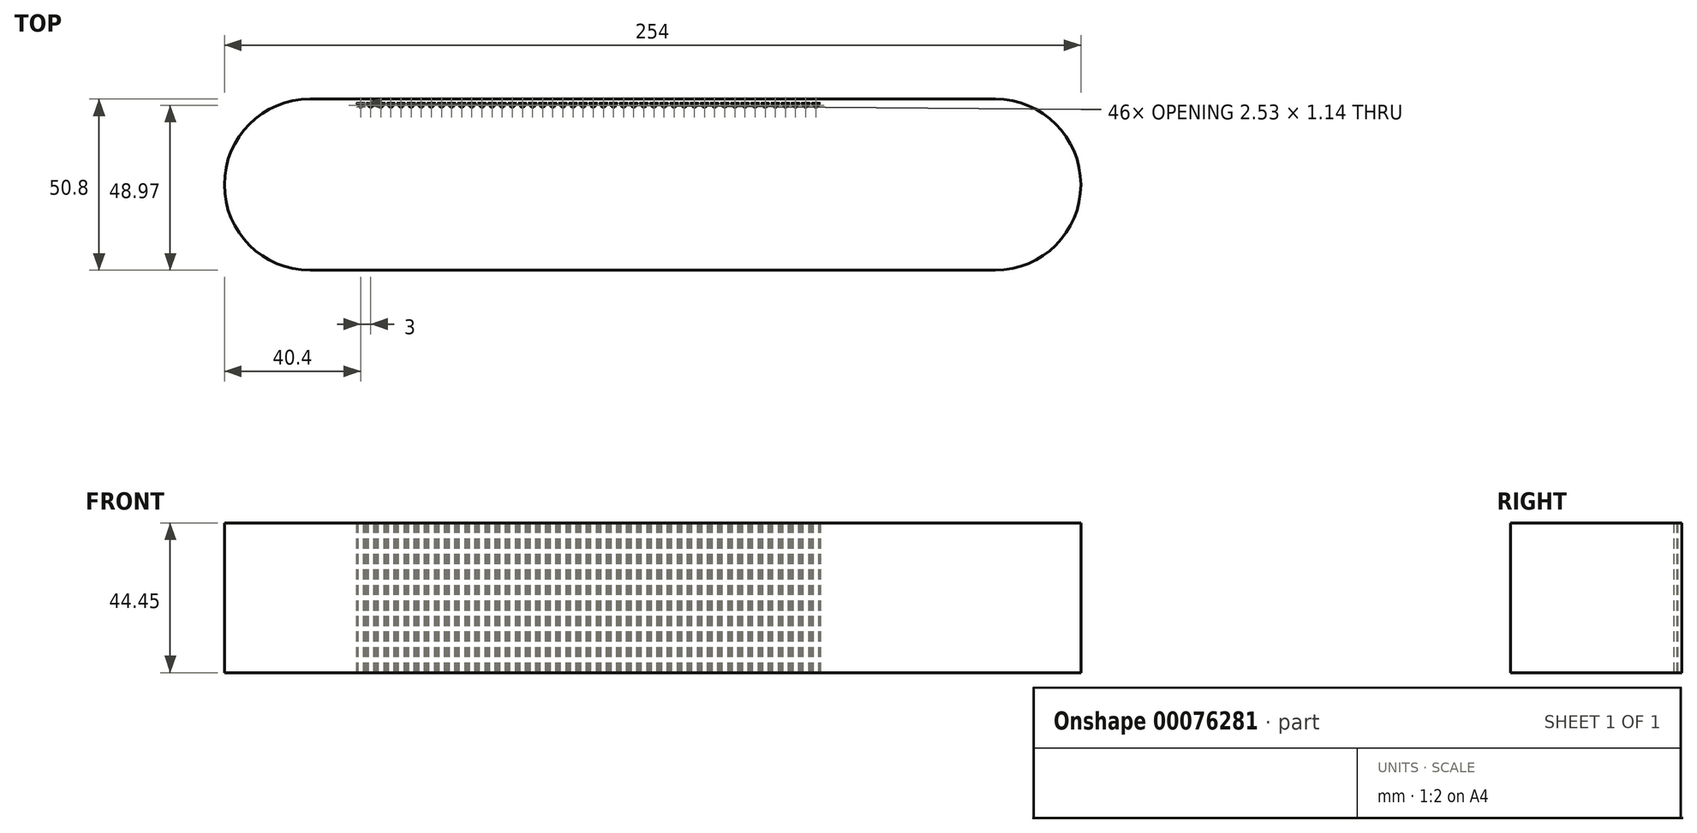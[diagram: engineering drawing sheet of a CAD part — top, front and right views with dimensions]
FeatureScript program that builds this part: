
annotation { "Feature Type Name" : "Feature", "Feature Type Description" : "" }
export const myFeature = defineFeature(function(context is Context, id is Id, definition is map)
    precondition{}
    {
        {
            var Q0;
            Q0=qCreatedBy(makeId("Top.planeOp"),FACE);
            var sketch = newSketch(context, id + "F0", { "sketchPlane" : qUnion([Q0])});
            skLineSegment(sketch, "E0.bottom", {"start": v(-101.6, -25.4) * mm, "end": v(101.6, -25.4) * mm});
            skLineSegment(sketch, "E0.top", {"start": v(-101.6, 25.4) * mm, "end": v(101.6, 25.4) * mm});
            skPoint(sketch, "E0.middle", {"position": v(0, 0) * mm});
            skArc(sketch, "E1", {"start": v(101.6, -25.4) * mm, "mid": v(127, 0) * mm, "end": v(101.6, 25.4) * mm});
            skArc(sketch, "E2", {"start": v(-101.6, 25.4) * mm, "mid": v(-127, 0) * mm, "end": v(-101.6, -25.4) * mm});
            skArc(sketch, "E3.0", {"start": v(-102.73, 24.11) * mm, "mid": v(-125.73, -0.57) * mm, "end": v(-101.6, -24.14) * mm});
            skLineSegment(sketch, "E3.1", {"start": v(-100.33, 24.14) * mm, "end": v(-99.87, 24.14) * mm});
            skArc(sketch, "E3.2", {"start": v(101.6, -24.14) * mm, "mid": v(125.74, 0) * mm, "end": v(101.6, 24.14) * mm});
            skLineSegment(sketch, "E3.3", {"start": v(-101.6, -24.14) * mm, "end": v(101.6, -24.14) * mm});
            skLineSegment(sketch, "E4", {"start": v(-101.6, 25.4) * mm, "end": v(-101.6, 23) * mm, "construction": true});
            skLineSegment(sketch, "E5", {"start": v(-101.6, 23) * mm, "end": v(-98.6, 23) * mm, "construction": true});
            skLineSegment(sketch, "E6", {"start": v(-98.6, 23) * mm, "end": v(-98.6, 23.85) * mm, "construction": true});
            skArc(sketch, "E7", {"start": v(-99.45, 23.78) * mm, "mid": v(-98.6, 23) * mm, "end": v(-97.75, 23.78) * mm});
            skLineSegment(sketch, "E8", {"start": v(-98.6, 23.85) * mm, "end": v(-101.6, 23.85) * mm, "construction": true});
            skArc(sketch, "E9", {"start": v(-102.45, 23.78) * mm, "mid": v(-101.6, 23) * mm, "end": v(-100.75, 23.78) * mm});
            skArc(sketch, "E10", {"start": v(-99.45, 23.78) * mm, "mid": v(-99.6, 24.03) * mm, "end": v(-99.87, 24.14) * mm});
            skArc(sketch, "E11.MirrorCS", {"start": v(-97.75, 23.78) * mm, "mid": v(-97.6, 24.03) * mm, "end": v(-97.33, 24.14) * mm});
            skLineSegment(sketch, "E12", {"start": v(-100.1, 23) * mm, "end": v(-100.1, 25.4) * mm, "construction": true});
            skArc(sketch, "E13.MirrorCS", {"start": v(-100.75, 23.78) * mm, "mid": v(-100.6, 24.03) * mm, "end": v(-100.33, 24.14) * mm});
            skArc(sketch, "E14.MirrorCS", {"start": v(-102.45, 23.78) * mm, "mid": v(-102.55, 23.98) * mm, "end": v(-102.73, 24.11) * mm});
            skPoint(sketch, "E15.orphan", {"position": v(-102.87, 24.14) * mm});
            skArc(sketch, "E16.1.0.0", {"start": v(-94.75, 23.78) * mm, "mid": v(-94.6, 24.03) * mm, "end": v(-94.33, 24.14) * mm});
            skArc(sketch, "E16.1.0.1", {"start": v(-96.45, 23.78) * mm, "mid": v(-95.6, 23) * mm, "end": v(-94.75, 23.78) * mm});
            skArc(sketch, "E16.1.0.2", {"start": v(-96.45, 23.78) * mm, "mid": v(-96.6, 24.03) * mm, "end": v(-96.87, 24.14) * mm});
            skArc(sketch, "E16.2.0.0", {"start": v(-91.75, 23.78) * mm, "mid": v(-91.6, 24.03) * mm, "end": v(-91.33, 24.14) * mm});
            skArc(sketch, "E16.2.0.1", {"start": v(-93.45, 23.78) * mm, "mid": v(-92.6, 23) * mm, "end": v(-91.75, 23.78) * mm});
            skArc(sketch, "E16.2.0.2", {"start": v(-93.45, 23.78) * mm, "mid": v(-93.6, 24.03) * mm, "end": v(-93.87, 24.14) * mm});
            skArc(sketch, "E16.3.0.0", {"start": v(-88.75, 23.78) * mm, "mid": v(-88.6, 24.03) * mm, "end": v(-88.33, 24.14) * mm});
            skArc(sketch, "E16.3.0.1", {"start": v(-90.45, 23.78) * mm, "mid": v(-89.6, 23) * mm, "end": v(-88.75, 23.78) * mm});
            skArc(sketch, "E16.3.0.2", {"start": v(-90.45, 23.78) * mm, "mid": v(-90.6, 24.03) * mm, "end": v(-90.87, 24.14) * mm});
            skArc(sketch, "E16.4.0.0", {"start": v(-85.75, 23.78) * mm, "mid": v(-85.6, 24.03) * mm, "end": v(-85.33, 24.14) * mm});
            skArc(sketch, "E16.4.0.1", {"start": v(-87.45, 23.78) * mm, "mid": v(-86.6, 23) * mm, "end": v(-85.75, 23.78) * mm});
            skArc(sketch, "E16.4.0.2", {"start": v(-87.45, 23.78) * mm, "mid": v(-87.6, 24.03) * mm, "end": v(-87.87, 24.14) * mm});
            skArc(sketch, "E16.5.0.0", {"start": v(-82.75, 23.78) * mm, "mid": v(-82.6, 24.03) * mm, "end": v(-82.33, 24.14) * mm});
            skArc(sketch, "E16.5.0.1", {"start": v(-84.45, 23.78) * mm, "mid": v(-83.6, 23) * mm, "end": v(-82.75, 23.78) * mm});
            skArc(sketch, "E16.5.0.2", {"start": v(-84.45, 23.78) * mm, "mid": v(-84.6, 24.03) * mm, "end": v(-84.87, 24.14) * mm});
            skArc(sketch, "E16.6.0.0", {"start": v(-79.75, 23.78) * mm, "mid": v(-79.6, 24.03) * mm, "end": v(-79.33, 24.14) * mm});
            skArc(sketch, "E16.6.0.1", {"start": v(-81.45, 23.78) * mm, "mid": v(-80.6, 23) * mm, "end": v(-79.75, 23.78) * mm});
            skArc(sketch, "E16.6.0.2", {"start": v(-81.45, 23.78) * mm, "mid": v(-81.6, 24.03) * mm, "end": v(-81.87, 24.14) * mm});
            skArc(sketch, "E16.7.0.0", {"start": v(-76.75, 23.78) * mm, "mid": v(-76.6, 24.03) * mm, "end": v(-76.33, 24.14) * mm});
            skArc(sketch, "E16.7.0.1", {"start": v(-78.45, 23.78) * mm, "mid": v(-77.6, 23) * mm, "end": v(-76.75, 23.78) * mm});
            skArc(sketch, "E16.7.0.2", {"start": v(-78.45, 23.78) * mm, "mid": v(-78.6, 24.03) * mm, "end": v(-78.87, 24.14) * mm});
            skArc(sketch, "E16.8.0.0", {"start": v(-73.75, 23.78) * mm, "mid": v(-73.6, 24.03) * mm, "end": v(-73.33, 24.14) * mm});
            skArc(sketch, "E16.8.0.1", {"start": v(-75.45, 23.78) * mm, "mid": v(-74.6, 23) * mm, "end": v(-73.75, 23.78) * mm});
            skArc(sketch, "E16.8.0.2", {"start": v(-75.45, 23.78) * mm, "mid": v(-75.6, 24.03) * mm, "end": v(-75.87, 24.14) * mm});
            skArc(sketch, "E16.9.0.0", {"start": v(-70.75, 23.78) * mm, "mid": v(-70.6, 24.03) * mm, "end": v(-70.33, 24.14) * mm});
            skArc(sketch, "E16.9.0.1", {"start": v(-72.45, 23.78) * mm, "mid": v(-71.6, 23) * mm, "end": v(-70.75, 23.78) * mm});
            skArc(sketch, "E16.9.0.2", {"start": v(-72.45, 23.78) * mm, "mid": v(-72.6, 24.03) * mm, "end": v(-72.87, 24.14) * mm});
            skArc(sketch, "E16.10.0.0", {"start": v(-67.75, 23.78) * mm, "mid": v(-67.6, 24.03) * mm, "end": v(-67.33, 24.14) * mm});
            skArc(sketch, "E16.10.0.1", {"start": v(-69.45, 23.78) * mm, "mid": v(-68.6, 23) * mm, "end": v(-67.75, 23.78) * mm});
            skArc(sketch, "E16.10.0.2", {"start": v(-69.45, 23.78) * mm, "mid": v(-69.6, 24.03) * mm, "end": v(-69.87, 24.14) * mm});
            skArc(sketch, "E16.11.0.0", {"start": v(-64.75, 23.78) * mm, "mid": v(-64.6, 24.03) * mm, "end": v(-64.33, 24.14) * mm});
            skArc(sketch, "E16.11.0.1", {"start": v(-66.45, 23.78) * mm, "mid": v(-65.6, 23) * mm, "end": v(-64.75, 23.78) * mm});
            skArc(sketch, "E16.11.0.2", {"start": v(-66.45, 23.78) * mm, "mid": v(-66.6, 24.03) * mm, "end": v(-66.87, 24.14) * mm});
            skArc(sketch, "E16.12.0.0", {"start": v(-61.75, 23.78) * mm, "mid": v(-61.6, 24.03) * mm, "end": v(-61.33, 24.14) * mm});
            skArc(sketch, "E16.12.0.1", {"start": v(-63.45, 23.78) * mm, "mid": v(-62.6, 23) * mm, "end": v(-61.75, 23.78) * mm});
            skArc(sketch, "E16.12.0.2", {"start": v(-63.45, 23.78) * mm, "mid": v(-63.6, 24.03) * mm, "end": v(-63.87, 24.14) * mm});
            skArc(sketch, "E16.13.0.0", {"start": v(-58.75, 23.78) * mm, "mid": v(-58.6, 24.03) * mm, "end": v(-58.33, 24.14) * mm});
            skArc(sketch, "E16.13.0.1", {"start": v(-60.45, 23.78) * mm, "mid": v(-59.6, 23) * mm, "end": v(-58.75, 23.78) * mm});
            skArc(sketch, "E16.13.0.2", {"start": v(-60.45, 23.78) * mm, "mid": v(-60.6, 24.03) * mm, "end": v(-60.87, 24.14) * mm});
            skArc(sketch, "E16.14.0.0", {"start": v(-55.75, 23.78) * mm, "mid": v(-55.6, 24.03) * mm, "end": v(-55.33, 24.14) * mm});
            skArc(sketch, "E16.14.0.1", {"start": v(-57.45, 23.78) * mm, "mid": v(-56.6, 23) * mm, "end": v(-55.75, 23.78) * mm});
            skArc(sketch, "E16.14.0.2", {"start": v(-57.45, 23.78) * mm, "mid": v(-57.6, 24.03) * mm, "end": v(-57.87, 24.14) * mm});
            skArc(sketch, "E16.15.0.0", {"start": v(-52.75, 23.78) * mm, "mid": v(-52.6, 24.03) * mm, "end": v(-52.33, 24.14) * mm});
            skArc(sketch, "E16.15.0.1", {"start": v(-54.45, 23.78) * mm, "mid": v(-53.6, 23) * mm, "end": v(-52.75, 23.78) * mm});
            skArc(sketch, "E16.15.0.2", {"start": v(-54.45, 23.78) * mm, "mid": v(-54.6, 24.03) * mm, "end": v(-54.87, 24.14) * mm});
            skArc(sketch, "E16.16.0.0", {"start": v(-49.75, 23.78) * mm, "mid": v(-49.6, 24.03) * mm, "end": v(-49.33, 24.14) * mm});
            skArc(sketch, "E16.16.0.1", {"start": v(-51.45, 23.78) * mm, "mid": v(-50.6, 23) * mm, "end": v(-49.75, 23.78) * mm});
            skArc(sketch, "E16.16.0.2", {"start": v(-51.45, 23.78) * mm, "mid": v(-51.6, 24.03) * mm, "end": v(-51.87, 24.14) * mm});
            skArc(sketch, "E16.17.0.0", {"start": v(-46.75, 23.78) * mm, "mid": v(-46.6, 24.03) * mm, "end": v(-46.33, 24.14) * mm});
            skArc(sketch, "E16.17.0.1", {"start": v(-48.45, 23.78) * mm, "mid": v(-47.6, 23) * mm, "end": v(-46.75, 23.78) * mm});
            skArc(sketch, "E16.17.0.2", {"start": v(-48.45, 23.78) * mm, "mid": v(-48.6, 24.03) * mm, "end": v(-48.87, 24.14) * mm});
            skArc(sketch, "E16.18.0.0", {"start": v(-43.75, 23.78) * mm, "mid": v(-43.6, 24.03) * mm, "end": v(-43.33, 24.14) * mm});
            skArc(sketch, "E16.18.0.1", {"start": v(-45.45, 23.78) * mm, "mid": v(-44.6, 23) * mm, "end": v(-43.75, 23.78) * mm});
            skArc(sketch, "E16.18.0.2", {"start": v(-45.45, 23.78) * mm, "mid": v(-45.6, 24.03) * mm, "end": v(-45.87, 24.14) * mm});
            skArc(sketch, "E16.19.0.0", {"start": v(-40.75, 23.78) * mm, "mid": v(-40.6, 24.03) * mm, "end": v(-40.33, 24.14) * mm});
            skArc(sketch, "E16.19.0.1", {"start": v(-42.45, 23.78) * mm, "mid": v(-41.6, 23) * mm, "end": v(-40.75, 23.78) * mm});
            skArc(sketch, "E16.19.0.2", {"start": v(-42.45, 23.78) * mm, "mid": v(-42.6, 24.03) * mm, "end": v(-42.87, 24.14) * mm});
            skArc(sketch, "E16.20.0.0", {"start": v(-37.75, 23.78) * mm, "mid": v(-37.6, 24.03) * mm, "end": v(-37.33, 24.14) * mm});
            skArc(sketch, "E16.20.0.1", {"start": v(-39.45, 23.78) * mm, "mid": v(-38.6, 23) * mm, "end": v(-37.75, 23.78) * mm});
            skArc(sketch, "E16.20.0.2", {"start": v(-39.45, 23.78) * mm, "mid": v(-39.6, 24.03) * mm, "end": v(-39.87, 24.14) * mm});
            skArc(sketch, "E16.21.0.0", {"start": v(-34.75, 23.78) * mm, "mid": v(-34.6, 24.03) * mm, "end": v(-34.33, 24.14) * mm});
            skArc(sketch, "E16.21.0.1", {"start": v(-36.45, 23.78) * mm, "mid": v(-35.6, 23) * mm, "end": v(-34.75, 23.78) * mm});
            skArc(sketch, "E16.21.0.2", {"start": v(-36.45, 23.78) * mm, "mid": v(-36.6, 24.03) * mm, "end": v(-36.87, 24.14) * mm});
            skArc(sketch, "E16.22.0.0", {"start": v(-31.75, 23.78) * mm, "mid": v(-31.6, 24.03) * mm, "end": v(-31.33, 24.14) * mm});
            skArc(sketch, "E16.22.0.1", {"start": v(-33.45, 23.78) * mm, "mid": v(-32.6, 23) * mm, "end": v(-31.75, 23.78) * mm});
            skArc(sketch, "E16.22.0.2", {"start": v(-33.45, 23.78) * mm, "mid": v(-33.6, 24.03) * mm, "end": v(-33.87, 24.14) * mm});
            skArc(sketch, "E16.23.0.0", {"start": v(-28.75, 23.78) * mm, "mid": v(-28.6, 24.03) * mm, "end": v(-28.33, 24.14) * mm});
            skArc(sketch, "E16.23.0.1", {"start": v(-30.45, 23.78) * mm, "mid": v(-29.6, 23) * mm, "end": v(-28.75, 23.78) * mm});
            skArc(sketch, "E16.23.0.2", {"start": v(-30.45, 23.78) * mm, "mid": v(-30.6, 24.03) * mm, "end": v(-30.87, 24.14) * mm});
            skArc(sketch, "E16.24.0.0", {"start": v(-25.75, 23.78) * mm, "mid": v(-25.6, 24.03) * mm, "end": v(-25.33, 24.14) * mm});
            skArc(sketch, "E16.24.0.1", {"start": v(-27.45, 23.78) * mm, "mid": v(-26.6, 23) * mm, "end": v(-25.75, 23.78) * mm});
            skArc(sketch, "E16.24.0.2", {"start": v(-27.45, 23.78) * mm, "mid": v(-27.6, 24.03) * mm, "end": v(-27.87, 24.14) * mm});
            skArc(sketch, "E16.25.0.0", {"start": v(-22.75, 23.78) * mm, "mid": v(-22.6, 24.03) * mm, "end": v(-22.33, 24.14) * mm});
            skArc(sketch, "E16.25.0.1", {"start": v(-24.45, 23.78) * mm, "mid": v(-23.6, 23) * mm, "end": v(-22.75, 23.78) * mm});
            skArc(sketch, "E16.25.0.2", {"start": v(-24.45, 23.78) * mm, "mid": v(-24.6, 24.03) * mm, "end": v(-24.87, 24.14) * mm});
            skArc(sketch, "E16.26.0.0", {"start": v(-19.75, 23.78) * mm, "mid": v(-19.6, 24.03) * mm, "end": v(-19.33, 24.14) * mm});
            skArc(sketch, "E16.26.0.1", {"start": v(-21.45, 23.78) * mm, "mid": v(-20.6, 23) * mm, "end": v(-19.75, 23.78) * mm});
            skArc(sketch, "E16.26.0.2", {"start": v(-21.45, 23.78) * mm, "mid": v(-21.6, 24.03) * mm, "end": v(-21.87, 24.14) * mm});
            skArc(sketch, "E16.27.0.0", {"start": v(-16.75, 23.78) * mm, "mid": v(-16.6, 24.03) * mm, "end": v(-16.33, 24.14) * mm});
            skArc(sketch, "E16.27.0.1", {"start": v(-18.45, 23.78) * mm, "mid": v(-17.6, 23) * mm, "end": v(-16.75, 23.78) * mm});
            skArc(sketch, "E16.27.0.2", {"start": v(-18.45, 23.78) * mm, "mid": v(-18.6, 24.03) * mm, "end": v(-18.87, 24.14) * mm});
            skArc(sketch, "E16.28.0.0", {"start": v(-13.75, 23.78) * mm, "mid": v(-13.6, 24.03) * mm, "end": v(-13.33, 24.14) * mm});
            skArc(sketch, "E16.28.0.1", {"start": v(-15.45, 23.78) * mm, "mid": v(-14.6, 23) * mm, "end": v(-13.75, 23.78) * mm});
            skArc(sketch, "E16.28.0.2", {"start": v(-15.45, 23.78) * mm, "mid": v(-15.6, 24.03) * mm, "end": v(-15.87, 24.14) * mm});
            skArc(sketch, "E16.29.0.0", {"start": v(-10.75, 23.78) * mm, "mid": v(-10.6, 24.03) * mm, "end": v(-10.33, 24.14) * mm});
            skArc(sketch, "E16.29.0.1", {"start": v(-12.45, 23.78) * mm, "mid": v(-11.6, 23) * mm, "end": v(-10.75, 23.78) * mm});
            skArc(sketch, "E16.29.0.2", {"start": v(-12.45, 23.78) * mm, "mid": v(-12.6, 24.03) * mm, "end": v(-12.87, 24.14) * mm});
            skArc(sketch, "E16.30.0.0", {"start": v(-7.75, 23.78) * mm, "mid": v(-7.6, 24.03) * mm, "end": v(-7.33, 24.14) * mm});
            skArc(sketch, "E16.30.0.1", {"start": v(-9.45, 23.78) * mm, "mid": v(-8.6, 23) * mm, "end": v(-7.75, 23.78) * mm});
            skArc(sketch, "E16.30.0.2", {"start": v(-9.45, 23.78) * mm, "mid": v(-9.6, 24.03) * mm, "end": v(-9.87, 24.14) * mm});
            skArc(sketch, "E16.31.0.0", {"start": v(-4.75, 23.78) * mm, "mid": v(-4.6, 24.03) * mm, "end": v(-4.33, 24.14) * mm});
            skArc(sketch, "E16.31.0.1", {"start": v(-6.45, 23.78) * mm, "mid": v(-5.6, 23) * mm, "end": v(-4.75, 23.78) * mm});
            skArc(sketch, "E16.31.0.2", {"start": v(-6.45, 23.78) * mm, "mid": v(-6.6, 24.03) * mm, "end": v(-6.87, 24.14) * mm});
            skArc(sketch, "E16.32.0.0", {"start": v(-1.75, 23.78) * mm, "mid": v(-1.6, 24.03) * mm, "end": v(-1.33, 24.14) * mm});
            skArc(sketch, "E16.32.0.1", {"start": v(-3.45, 23.78) * mm, "mid": v(-2.6, 23) * mm, "end": v(-1.75, 23.78) * mm});
            skArc(sketch, "E16.32.0.2", {"start": v(-3.45, 23.78) * mm, "mid": v(-3.6, 24.03) * mm, "end": v(-3.87, 24.14) * mm});
            skArc(sketch, "E16.33.0.0", {"start": v(1.25, 23.78) * mm, "mid": v(1.4, 24.03) * mm, "end": v(1.67, 24.14) * mm});
            skArc(sketch, "E16.33.0.1", {"start": v(-0.45, 23.78) * mm, "mid": v(0.4, 23) * mm, "end": v(1.25, 23.78) * mm});
            skArc(sketch, "E16.33.0.2", {"start": v(-0.45, 23.78) * mm, "mid": v(-0.6, 24.03) * mm, "end": v(-0.87, 24.14) * mm});
            skArc(sketch, "E16.34.0.0", {"start": v(4.25, 23.78) * mm, "mid": v(4.4, 24.03) * mm, "end": v(4.67, 24.14) * mm});
            skArc(sketch, "E16.34.0.1", {"start": v(2.55, 23.78) * mm, "mid": v(3.4, 23) * mm, "end": v(4.25, 23.78) * mm});
            skArc(sketch, "E16.34.0.2", {"start": v(2.55, 23.78) * mm, "mid": v(2.4, 24.03) * mm, "end": v(2.13, 24.14) * mm});
            skArc(sketch, "E16.35.0.0", {"start": v(7.25, 23.78) * mm, "mid": v(7.4, 24.03) * mm, "end": v(7.67, 24.14) * mm});
            skArc(sketch, "E16.35.0.1", {"start": v(5.55, 23.78) * mm, "mid": v(6.4, 23) * mm, "end": v(7.25, 23.78) * mm});
            skArc(sketch, "E16.35.0.2", {"start": v(5.55, 23.78) * mm, "mid": v(5.4, 24.03) * mm, "end": v(5.13, 24.14) * mm});
            skArc(sketch, "E16.36.0.0", {"start": v(10.25, 23.78) * mm, "mid": v(10.4, 24.03) * mm, "end": v(10.67, 24.14) * mm});
            skArc(sketch, "E16.36.0.1", {"start": v(8.55, 23.78) * mm, "mid": v(9.4, 23) * mm, "end": v(10.25, 23.78) * mm});
            skArc(sketch, "E16.36.0.2", {"start": v(8.55, 23.78) * mm, "mid": v(8.4, 24.03) * mm, "end": v(8.13, 24.14) * mm});
            skArc(sketch, "E16.37.0.0", {"start": v(13.25, 23.78) * mm, "mid": v(13.4, 24.03) * mm, "end": v(13.67, 24.14) * mm});
            skArc(sketch, "E16.37.0.1", {"start": v(11.55, 23.78) * mm, "mid": v(12.4, 23) * mm, "end": v(13.25, 23.78) * mm});
            skArc(sketch, "E16.37.0.2", {"start": v(11.55, 23.78) * mm, "mid": v(11.4, 24.03) * mm, "end": v(11.13, 24.14) * mm});
            skArc(sketch, "E16.38.0.0", {"start": v(16.25, 23.78) * mm, "mid": v(16.4, 24.03) * mm, "end": v(16.67, 24.14) * mm});
            skArc(sketch, "E16.38.0.1", {"start": v(14.55, 23.78) * mm, "mid": v(15.4, 23) * mm, "end": v(16.25, 23.78) * mm});
            skArc(sketch, "E16.38.0.2", {"start": v(14.55, 23.78) * mm, "mid": v(14.4, 24.03) * mm, "end": v(14.13, 24.14) * mm});
            skArc(sketch, "E16.39.0.0", {"start": v(19.25, 23.78) * mm, "mid": v(19.4, 24.03) * mm, "end": v(19.67, 24.14) * mm});
            skArc(sketch, "E16.39.0.1", {"start": v(17.55, 23.78) * mm, "mid": v(18.4, 23) * mm, "end": v(19.25, 23.78) * mm});
            skArc(sketch, "E16.39.0.2", {"start": v(17.55, 23.78) * mm, "mid": v(17.4, 24.03) * mm, "end": v(17.13, 24.14) * mm});
            skArc(sketch, "E16.40.0.0", {"start": v(22.25, 23.78) * mm, "mid": v(22.4, 24.03) * mm, "end": v(22.67, 24.14) * mm});
            skArc(sketch, "E16.40.0.1", {"start": v(20.55, 23.78) * mm, "mid": v(21.4, 23) * mm, "end": v(22.25, 23.78) * mm});
            skArc(sketch, "E16.40.0.2", {"start": v(20.55, 23.78) * mm, "mid": v(20.4, 24.03) * mm, "end": v(20.13, 24.14) * mm});
            skArc(sketch, "E16.41.0.0", {"start": v(25.25, 23.78) * mm, "mid": v(25.4, 24.03) * mm, "end": v(25.67, 24.14) * mm});
            skArc(sketch, "E16.41.0.1", {"start": v(23.55, 23.78) * mm, "mid": v(24.4, 23) * mm, "end": v(25.25, 23.78) * mm});
            skArc(sketch, "E16.41.0.2", {"start": v(23.55, 23.78) * mm, "mid": v(23.4, 24.03) * mm, "end": v(23.13, 24.14) * mm});
            skArc(sketch, "E16.42.0.0", {"start": v(28.25, 23.78) * mm, "mid": v(28.4, 24.03) * mm, "end": v(28.67, 24.14) * mm});
            skArc(sketch, "E16.42.0.1", {"start": v(26.55, 23.78) * mm, "mid": v(27.4, 23) * mm, "end": v(28.25, 23.78) * mm});
            skArc(sketch, "E16.42.0.2", {"start": v(26.55, 23.78) * mm, "mid": v(26.4, 24.03) * mm, "end": v(26.13, 24.14) * mm});
            skArc(sketch, "E16.43.0.0", {"start": v(31.25, 23.78) * mm, "mid": v(31.4, 24.03) * mm, "end": v(31.67, 24.14) * mm});
            skArc(sketch, "E16.43.0.1", {"start": v(29.55, 23.78) * mm, "mid": v(30.4, 23) * mm, "end": v(31.25, 23.78) * mm});
            skArc(sketch, "E16.43.0.2", {"start": v(29.55, 23.78) * mm, "mid": v(29.4, 24.03) * mm, "end": v(29.13, 24.14) * mm});
            skArc(sketch, "E16.44.0.0", {"start": v(34.25, 23.78) * mm, "mid": v(34.4, 24.03) * mm, "end": v(34.67, 24.14) * mm});
            skArc(sketch, "E16.44.0.1", {"start": v(32.55, 23.78) * mm, "mid": v(33.4, 23) * mm, "end": v(34.25, 23.78) * mm});
            skArc(sketch, "E16.44.0.2", {"start": v(32.55, 23.78) * mm, "mid": v(32.4, 24.03) * mm, "end": v(32.13, 24.14) * mm});
            skArc(sketch, "E16.45.0.0", {"start": v(37.25, 23.78) * mm, "mid": v(37.4, 24.03) * mm, "end": v(37.67, 24.14) * mm});
            skArc(sketch, "E16.45.0.1", {"start": v(35.55, 23.78) * mm, "mid": v(36.4, 23) * mm, "end": v(37.25, 23.78) * mm});
            skArc(sketch, "E16.45.0.2", {"start": v(35.55, 23.78) * mm, "mid": v(35.4, 24.03) * mm, "end": v(35.13, 24.14) * mm});
            skArc(sketch, "E16.46.0.0", {"start": v(40.25, 23.78) * mm, "mid": v(40.4, 24.03) * mm, "end": v(40.67, 24.14) * mm});
            skArc(sketch, "E16.46.0.1", {"start": v(38.55, 23.78) * mm, "mid": v(39.4, 23) * mm, "end": v(40.25, 23.78) * mm});
            skArc(sketch, "E16.46.0.2", {"start": v(38.55, 23.78) * mm, "mid": v(38.4, 24.03) * mm, "end": v(38.13, 24.14) * mm});
            skArc(sketch, "E16.47.0.0", {"start": v(43.25, 23.78) * mm, "mid": v(43.4, 24.03) * mm, "end": v(43.67, 24.14) * mm});
            skArc(sketch, "E16.47.0.1", {"start": v(41.55, 23.78) * mm, "mid": v(42.4, 23) * mm, "end": v(43.25, 23.78) * mm});
            skArc(sketch, "E16.47.0.2", {"start": v(41.55, 23.78) * mm, "mid": v(41.4, 24.03) * mm, "end": v(41.13, 24.14) * mm});
            skArc(sketch, "E16.48.0.0", {"start": v(46.25, 23.78) * mm, "mid": v(46.4, 24.03) * mm, "end": v(46.67, 24.14) * mm});
            skArc(sketch, "E16.48.0.1", {"start": v(44.55, 23.78) * mm, "mid": v(45.4, 23) * mm, "end": v(46.25, 23.78) * mm});
            skArc(sketch, "E16.48.0.2", {"start": v(44.55, 23.78) * mm, "mid": v(44.4, 24.03) * mm, "end": v(44.13, 24.14) * mm});
            skArc(sketch, "E16.49.0.0", {"start": v(49.25, 23.78) * mm, "mid": v(49.4, 24.03) * mm, "end": v(49.67, 24.14) * mm});
            skArc(sketch, "E16.49.0.1", {"start": v(47.55, 23.78) * mm, "mid": v(48.4, 23) * mm, "end": v(49.25, 23.78) * mm});
            skArc(sketch, "E16.49.0.2", {"start": v(47.55, 23.78) * mm, "mid": v(47.4, 24.03) * mm, "end": v(47.13, 24.14) * mm});
            skLineSegment(sketch, "E16.direction1", {"start": v(-98.6, 23.85) * mm, "end": v(-95.6, 23.85) * mm, "construction": true});
            skLineSegment(sketch, "E17.trimOffspring", {"start": v(-94.33, 24.14) * mm, "end": v(-93.87, 24.14) * mm});
            skLineSegment(sketch, "E18.trimOffspring", {"start": v(-88.33, 24.14) * mm, "end": v(101.6, 24.14) * mm});
            skLineSegment(sketch, "E19", {"start": v(-91.33, 24.14) * mm, "end": v(-90.87, 24.14) * mm});
            skSolve(sketch);
        }
        {
            var Q0;
            Q0=makeQuery(id+"F0.imprint","IMPRINT",FACE,{"disambiguationData":[TD([[makeQuery(id+"F0.imprint","IMPRINT",EDGE,{"derivedFrom":sQuery(id+"F0.wireOp",EDGE,"E0.bottom")}),1.0]])]});
            extrude(context, id + "F1", {"entities" : qUnion([Q0]), "depth" : 44.45 * mm});
        }
    });
